# Revit family: KingswayGroup_PprTwlDspnsrs_Anti-LigaturePaperTowelDispenserRecessed
name_source: partatom
category: Specialty Equipment
units: mm (PartAtom-declared; Revit-internal decimal feet)

## family parameters
Always vertical = Yes
Cut with Voids When Loaded = No
Part Type = Normal
Room Calculation Point = No
Round Connector Dimension = Use Diameter
Shared = No
Work Plane-Based = No

## types (1)
- KingswayGroup_PprTwlDspnsrs_Anti-LigaturePaperTowelDispenserRecessed
    AssetType = Fixed
    BIMObjectName = KingswayGroup_PaperTowelDispensers_Anti-LigaturePaperTowelDispenserRecessed
    Category = Pr_40_70_22_62:Paper towel dispensers
    Color = For full range of available finishes and colours, contact Kingsway Group
    Default Elevation = 0 mm  [stored 0 ft]
    Description = Recessed Paper Towel Dispensers
    DispenserMaterial = NBS_Concept
    DurationUnit = year
    Features = A secure-locking paper towel dispenser manufactured from stainless steel for a durable and anti-ligature means of dispensing paper towels. Recessed and well styled, the KG11 Anti-Ligature Paper Towel Dispenser provides a modern and robust solution for challenging environments, helping to reduce risk and improve patient safety.
    Finish = For full range of available finishes and colours, contact Kingsway Group
    Grade = 316
    Manufacturer = Kingsway Group
    ManufacturerName = Kingsway Group
    ManufacturerURL = https://kingswaygroupglobal.com
    Material = Stainless Steel
    Model = KG11
    ModelNumber = KG11
    ModelReference = Anti-Ligature Paper Towel Dispenser (Recessed)
    Name = PaperTowelDispensers_Anti-LigaturePaperTowelDispenserRecessed_KG11_KingswayGroup
    NominalHeight = 394 mm
    NominalLength = 356 mm
    NominalWidth = 116 mm  [stored 0.380577 ft]
    ProductInformation = https://kingswaygroupglobal.com
    Size = 355.6 x 393.7 x 116 mm
    URL = https://kingswaygroupglobal.com
    Uniclass2015Code = Pr_40_70_22_62
    Uniclass2015Title = Paper towel dispensers
    Uniclass2015Version = Products v1.36
    Version = 1
    WarrantyDescription = 5-Year Guarantee *For faulty manufacture and not for damage
    WarrantyDurationParts = 5
    WarrantyDurationUnit = year

note: [stored X ft] marks values corroborated as IEEE doubles in the binary element streams (Revit-internal decimal feet)

## geometry (parser evidence)
native form markers: Sweep x2
no freeform markers — native parametric forms only
